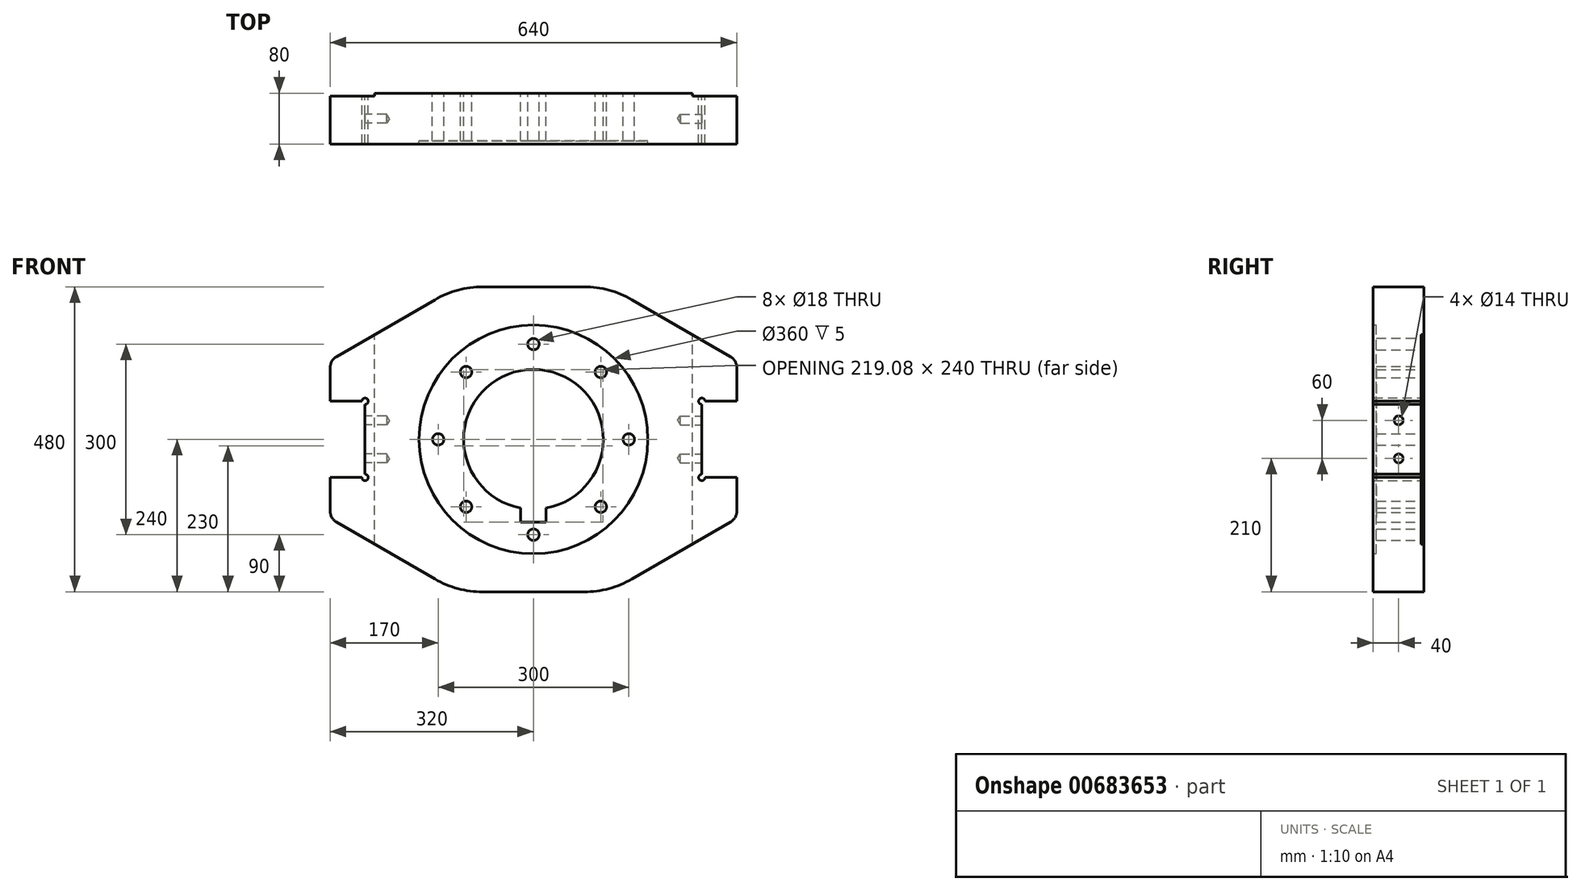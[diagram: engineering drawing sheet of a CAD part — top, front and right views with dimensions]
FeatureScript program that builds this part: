
annotation { "Feature Type Name" : "Feature", "Feature Type Description" : "" }
export const myFeature = defineFeature(function(context is Context, id is Id, definition is map)
    precondition{}
    {
        {
            var Q0;
            Q0=qCreatedBy(makeId("Front.planeOp"),FACE);
            var sketch = newSketch(context, id + "F0", { "sketchPlane" : qUnion([Q0])});
            skArc(sketch, "E0", {"start": v(80, -240) * mm, "mid": v(118.88, -234.87) * mm, "end": v(155.1, -219.84) * mm});
            skLineSegment(sketch, "E1", {"start": v(80, -240) * mm, "end": v(-80, -240) * mm});
            skArc(sketch, "E2", {"start": v(-155.1, -219.84) * mm, "mid": v(-118.88, -234.87) * mm, "end": v(-80, -240) * mm});
            skArc(sketch, "E3", {"start": v(-270, -60) * mm, "mid": v(-261.46, -63.54) * mm, "end": v(-265, -55) * mm});
            skLineSegment(sketch, "E4", {"start": v(-265, -55) * mm, "end": v(-265, 55) * mm});
            skArc(sketch, "E5", {"start": v(-265, 55) * mm, "mid": v(-261.46, 63.54) * mm, "end": v(-270, 60) * mm});
            skLineSegment(sketch, "E6", {"start": v(-320, 60) * mm, "end": v(-270, 60) * mm});
            skLineSegment(sketch, "E7", {"start": v(-320, 113) * mm, "end": v(-320, 60) * mm});
            skArc(sketch, "E8", {"start": v(-310, 130.32) * mm, "mid": v(-317.32, 123) * mm, "end": v(-320, 113) * mm});
            skLineSegment(sketch, "E9", {"start": v(-155.1, 219.84) * mm, "end": v(-310, 130.32) * mm});
            skArc(sketch, "E10", {"start": v(-80, 240) * mm, "mid": v(-118.88, 234.87) * mm, "end": v(-155.1, 219.84) * mm});
            skLineSegment(sketch, "E11", {"start": v(80, 240) * mm, "end": v(-80, 240) * mm});
            skArc(sketch, "E12", {"start": v(155.1, 219.84) * mm, "mid": v(118.88, 234.87) * mm, "end": v(80, 240) * mm});
            skLineSegment(sketch, "E13", {"start": v(320, 113) * mm, "end": v(320, 60) * mm});
            skLineSegment(sketch, "E14", {"start": v(320, 60) * mm, "end": v(270, 60) * mm});
            skArc(sketch, "E15", {"start": v(270, 60) * mm, "mid": v(261.46, 63.54) * mm, "end": v(265, 55) * mm});
            skLineSegment(sketch, "E16", {"start": v(265, -55) * mm, "end": v(265, 55) * mm});
            skArc(sketch, "E17", {"start": v(265, -55) * mm, "mid": v(261.46, -63.54) * mm, "end": v(270, -60) * mm});
            skLineSegment(sketch, "E18", {"start": v(320, -60) * mm, "end": v(270, -60) * mm});
            skLineSegment(sketch, "E19", {"start": v(320, -113) * mm, "end": v(320, -60) * mm});
            skLineSegment(sketch, "E20", {"start": v(-20, -130) * mm, "end": v(20, -130) * mm});
            skLineSegment(sketch, "E21", {"start": v(20, -130) * mm, "end": v(20, -108.17) * mm});
            skArc(sketch, "E22", {"start": v(20, -108.17) * mm, "mid": v(0, 110) * mm, "end": v(-20, -108.17) * mm});
            skLineSegment(sketch, "E23", {"start": v(-20, -108.17) * mm, "end": v(-20, -130) * mm});
            skCircle(sketch, "E24", {"center": v(150, 0) * mm, "radius": 9 * mm});
            skCircle(sketch, "E25", {"center": v(106.07, 106.07) * mm, "radius": 9 * mm});
            skCircle(sketch, "E26", {"center": v(0, 150) * mm, "radius": 9 * mm});
            skCircle(sketch, "E27", {"center": v(-106.07, 106.07) * mm, "radius": 9 * mm});
            skCircle(sketch, "E28", {"center": v(-150, 0) * mm, "radius": 9 * mm});
            skCircle(sketch, "E29", {"center": v(-106.07, -106.07) * mm, "radius": 9 * mm});
            skCircle(sketch, "E30", {"center": v(0, -150) * mm, "radius": 9 * mm});
            skCircle(sketch, "E31", {"center": v(106.07, -106.07) * mm, "radius": 9 * mm});
            skCircle(sketch, "E32", {"center": v(0, 0) * mm, "radius": 180 * mm});
            skArc(sketch, "E33", {"start": v(310, -130.32) * mm, "mid": v(317.32, -123) * mm, "end": v(320, -113) * mm});
            skLineSegment(sketch, "E34", {"start": v(155.1, -219.84) * mm, "end": v(310, -130.32) * mm});
            skLineSegment(sketch, "E35", {"start": v(155.1, 219.84) * mm, "end": v(310, 130.32) * mm});
            skArc(sketch, "E36", {"start": v(320, 113) * mm, "mid": v(317.32, 123) * mm, "end": v(310, 130.32) * mm});
            skLineSegment(sketch, "E37", {"start": v(-155.1, -219.84) * mm, "end": v(-310, -130.32) * mm});
            skArc(sketch, "E38", {"start": v(-320, -113) * mm, "mid": v(-317.32, -123) * mm, "end": v(-310, -130.32) * mm});
            skLineSegment(sketch, "E39", {"start": v(-320, -113) * mm, "end": v(-320, -60) * mm});
            skLineSegment(sketch, "E40", {"start": v(-320, -60) * mm, "end": v(-270, -60) * mm});
            skSolve(sketch);
        }
        {
            var Q0;
            Q0=makeQuery(id+"F0.imprint","IMPRINT",FACE,{"disambiguationData":[TD([[makeQuery(id+"F0.imprint","IMPRINT",EDGE,{"derivedFrom":sQuery(id+"F0.wireOp",EDGE,"E0")}),1.0]])]});
            extrude(context, id + "F1", {"entities" : qUnion([Q0]), "depth" : 80 * mm, "offsetDistance" : 25 * mm});
        }
        {
            var Q0;
            Q0=makeQuery(id+"F0.imprint","IMPRINT",FACE,{"disambiguationData":[TD([[makeQuery(id+"F0.imprint","IMPRINT",EDGE,{"derivedFrom":sQuery(id+"F0.wireOp",EDGE,"E20")}),-1.0]])]});
            extrude(context, id + "F2", {"entities" : qUnion([Q0]), "operationType" : NewBodyOperationType.ADD, "depth" : 75 * mm, "offsetDistance" : 25 * mm});
        }
        {
            var Q0;
            Q0=makeQuery(id+"F0.imprint","IMPRINT",FACE,{"disambiguationData":[TD([[makeQuery(id+"F0.imprint","IMPRINT",EDGE,{"derivedFrom":sQuery(id+"F0.wireOp",EDGE,"E0")}),1.0]])]});
            var sketch = newSketch(context, id + "F3", { "sketchPlane" : qUnion([Q0])});
            skLineSegment(sketch, "E41", {"start": v(250, -326.84) * mm, "end": v(250, 358.7) * mm});
            skLineSegment(sketch, "E42", {"start": v(250, -326.84) * mm, "end": v(360.02, -326.84) * mm});
            skLineSegment(sketch, "E43", {"start": v(360.02, -326.84) * mm, "end": v(360.02, 358.7) * mm});
            skLineSegment(sketch, "E44", {"start": v(360.02, 358.7) * mm, "end": v(250, 358.7) * mm});
            skLineSegment(sketch, "E45.MirrorCS", {"start": v(-360.02, 358.7) * mm, "end": v(-250, 358.7) * mm});
            skLineSegment(sketch, "E46.MirrorCS", {"start": v(-360.02, -326.84) * mm, "end": v(-360.02, 358.7) * mm});
            skLineSegment(sketch, "E47.MirrorCS", {"start": v(-250, -326.84) * mm, "end": v(-360.02, -326.84) * mm});
            skLineSegment(sketch, "E48", {"start": v(-250, -326.84) * mm, "end": v(-250, 358.7) * mm});
            skSolve(sketch);
        }
        {
            var Q0;
            Q0=makeQuery(id+"F3.imprint","IMPRINT",FACE,{"disambiguationData":[TD([[makeQuery(id+"F3.imprint","IMPRINT",EDGE,{"derivedFrom":makeQuery(id+"F0.imprint","IMPRINT",EDGE,{"derivedFrom":sQuery(id+"F0.wireOp",EDGE,"E13")})}),-1.0]])]});
            var Q1;
            Q1=makeQuery(id+"F3.imprint","IMPRINT",FACE,{"disambiguationData":[TD([[makeQuery(id+"F3.imprint","IMPRINT",EDGE,{"derivedFrom":makeQuery(id+"F0.imprint","IMPRINT",EDGE,{"derivedFrom":sQuery(id+"F0.wireOp",EDGE,"E3")})}),-1.0]])]});
            extrude(context, id + "F4", {"entities" : qUnion([Q0, Q1]), "operationType" : NewBodyOperationType.REMOVE, "depth" : 5 * mm, "offsetDistance" : 25 * mm});
        }
        {
            var Q0;
            Q0=makeQuery(id+"F1.opExtrude","SWEPT_FACE",FACE,{"disambiguationData":[OSD([sQuery(id+"F0.wireOp",EDGE,"E4")])]});
            var sketch = newSketch(context, id + "F5", { "sketchPlane" : qUnion([Q0])});
            skPoint(sketch, "E49", {"position": v(40, -30) * mm});
            skPoint(sketch, "E50", {"position": v(40, 30) * mm});
            skSolve(sketch);
        }
        {
            var Q0;
            Q0=sQuery(id+"F5.wireOp",VERTEX,"E49");
            var Q1;
            Q1=sQuery(id+"F5.wireOp",VERTEX,"E50");
            var Q2;
            Q2=makeQuery(id+"F1.opExtrude","SWEPT_BODY",BODY,{"disambiguationData":[OSD([sQuery(id+"F0.wireOp",EDGE,"E0"),sQuery(id+"F0.wireOp",EDGE,"E1"),sQuery(id+"F0.wireOp",EDGE,"E2"),sQuery(id+"F0.wireOp",EDGE,"E3"),sQuery(id+"F0.wireOp",EDGE,"E4"),sQuery(id+"F0.wireOp",EDGE,"E5"),sQuery(id+"F0.wireOp",EDGE,"E6"),sQuery(id+"F0.wireOp",EDGE,"E7"),sQuery(id+"F0.wireOp",EDGE,"E8"),sQuery(id+"F0.wireOp",EDGE,"E9"),sQuery(id+"F0.wireOp",EDGE,"E10"),sQuery(id+"F0.wireOp",EDGE,"E11"),sQuery(id+"F0.wireOp",EDGE,"E12"),sQuery(id+"F0.wireOp",EDGE,"E13"),sQuery(id+"F0.wireOp",EDGE,"E14"),sQuery(id+"F0.wireOp",EDGE,"E15"),sQuery(id+"F0.wireOp",EDGE,"E16"),sQuery(id+"F0.wireOp",EDGE,"E17"),sQuery(id+"F0.wireOp",EDGE,"E18"),sQuery(id+"F0.wireOp",EDGE,"E19"),sQuery(id+"F0.wireOp",EDGE,"E32"),sQuery(id+"F0.wireOp",EDGE,"E33"),sQuery(id+"F0.wireOp",EDGE,"E34"),sQuery(id+"F0.wireOp",EDGE,"E35"),sQuery(id+"F0.wireOp",EDGE,"E36"),sQuery(id+"F0.wireOp",EDGE,"E37"),sQuery(id+"F0.wireOp",EDGE,"E38"),sQuery(id+"F0.wireOp",EDGE,"E39"),sQuery(id+"F0.wireOp",EDGE,"E40")])]});
            hole(context, id + "F6", {"style" : HoleStyle.SIMPLE, "endStyle" : HoleEndStyle.BLIND, "standardTappedOrClearance" : lookupTablePath({ "standard" : "ISO", "engagement" : "75%", "pitch" : "2 mm", "size" : "M16", "type" : "Tapped" }), "standardBlindInLast" : lookupTablePath({ "standard" : "ISO", "engagement" : "75%", "pitch" : "2 mm", "size" : "M16", "type" : "Tapped" }), "holeDiameter" : 14 * mm, "majorDiameter" : 16 * mm, "showTappedDepth" : true, "holeDepth" : 34 * mm, "isTappedThrough" : true, "tappedDepth" : 30 * mm, "tapClearance" : 2, "locations" : qUnion([Q0, Q1]), "scope" : qUnion([Q2])});
        }
        {
            var Q0;
            Q0=makeQuery(id+"F1.opExtrude","SWEPT_FACE",FACE,{"disambiguationData":[OSD([sQuery(id+"F0.wireOp",EDGE,"E16")])]});
            var sketch = newSketch(context, id + "F7", { "sketchPlane" : qUnion([Q0])});
            skPoint(sketch, "E51", {"position": v(-40, -30) * mm});
            skPoint(sketch, "E52", {"position": v(-40, 30) * mm});
            skSolve(sketch);
        }
        {
            var Q0;
            Q0=sQuery(id+"F7.wireOp",VERTEX,"E51");
            var Q1;
            Q1=sQuery(id+"F7.wireOp",VERTEX,"E52");
            var Q2;
            Q2=makeQuery(id+"F1.opExtrude","SWEPT_BODY",BODY,{"disambiguationData":[OSD([sQuery(id+"F0.wireOp",EDGE,"E0"),sQuery(id+"F0.wireOp",EDGE,"E1"),sQuery(id+"F0.wireOp",EDGE,"E2"),sQuery(id+"F0.wireOp",EDGE,"E3"),sQuery(id+"F0.wireOp",EDGE,"E4"),sQuery(id+"F0.wireOp",EDGE,"E5"),sQuery(id+"F0.wireOp",EDGE,"E6"),sQuery(id+"F0.wireOp",EDGE,"E7"),sQuery(id+"F0.wireOp",EDGE,"E8"),sQuery(id+"F0.wireOp",EDGE,"E9"),sQuery(id+"F0.wireOp",EDGE,"E10"),sQuery(id+"F0.wireOp",EDGE,"E11"),sQuery(id+"F0.wireOp",EDGE,"E12"),sQuery(id+"F0.wireOp",EDGE,"E13"),sQuery(id+"F0.wireOp",EDGE,"E14"),sQuery(id+"F0.wireOp",EDGE,"E15"),sQuery(id+"F0.wireOp",EDGE,"E16"),sQuery(id+"F0.wireOp",EDGE,"E17"),sQuery(id+"F0.wireOp",EDGE,"E18"),sQuery(id+"F0.wireOp",EDGE,"E19"),sQuery(id+"F0.wireOp",EDGE,"E32"),sQuery(id+"F0.wireOp",EDGE,"E33"),sQuery(id+"F0.wireOp",EDGE,"E34"),sQuery(id+"F0.wireOp",EDGE,"E35"),sQuery(id+"F0.wireOp",EDGE,"E36"),sQuery(id+"F0.wireOp",EDGE,"E37"),sQuery(id+"F0.wireOp",EDGE,"E38"),sQuery(id+"F0.wireOp",EDGE,"E39"),sQuery(id+"F0.wireOp",EDGE,"E40")])]});
            hole(context, id + "F8", {"style" : HoleStyle.SIMPLE, "endStyle" : HoleEndStyle.BLIND, "standardTappedOrClearance" : lookupTablePath({ "standard" : "ISO", "engagement" : "75%", "pitch" : "2 mm", "size" : "M16", "type" : "Tapped" }), "standardBlindInLast" : lookupTablePath({ "standard" : "ISO", "engagement" : "75%", "pitch" : "2 mm", "size" : "M16", "type" : "Tapped" }), "holeDiameter" : 14 * mm, "majorDiameter" : 16 * mm, "showTappedDepth" : true, "holeDepth" : 34 * mm, "isTappedThrough" : true, "tappedDepth" : 30 * mm, "tapClearance" : 2, "locations" : qUnion([Q0, Q1]), "scope" : qUnion([Q2])});
        }
    });
